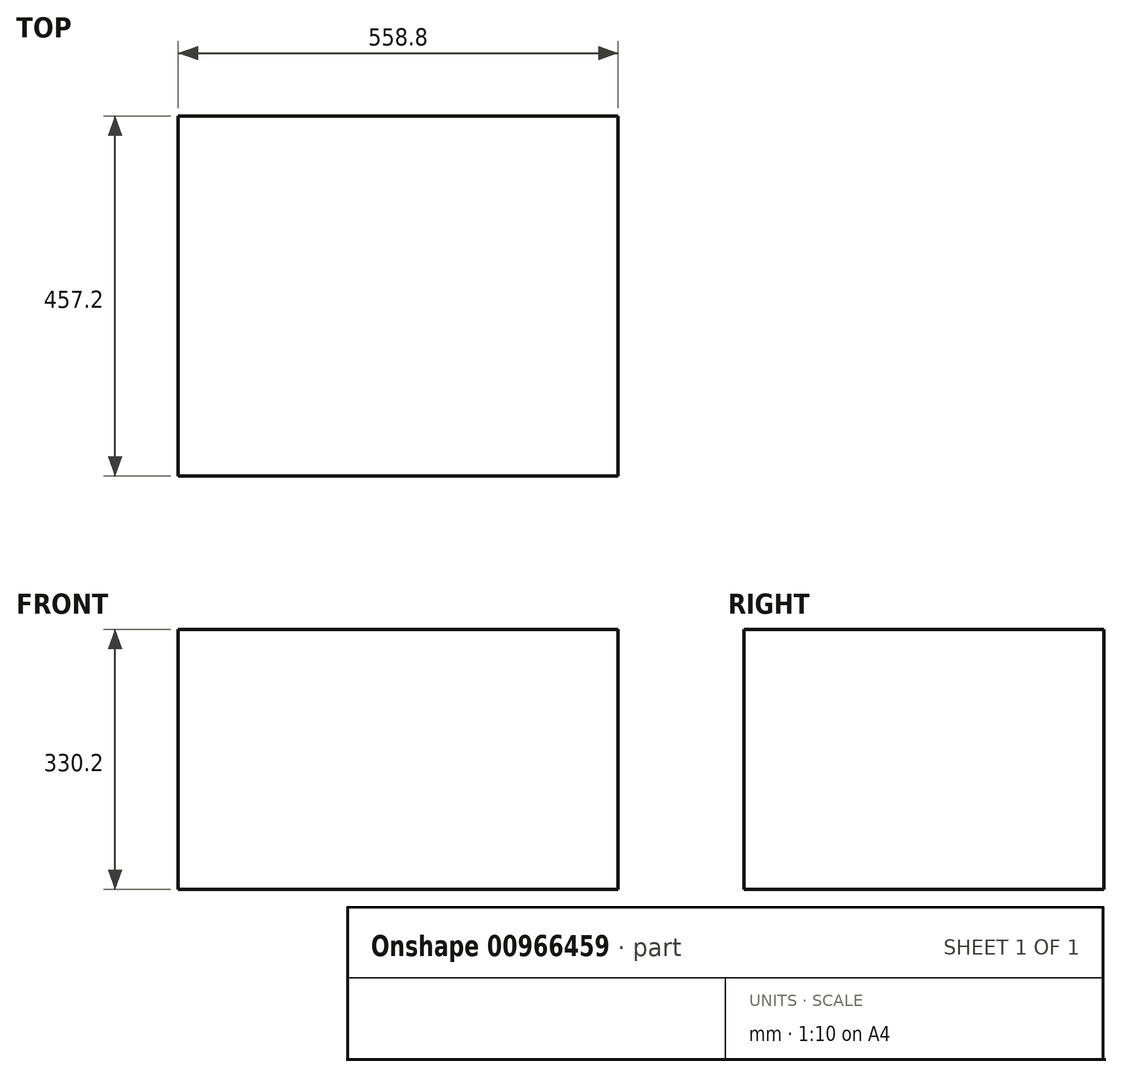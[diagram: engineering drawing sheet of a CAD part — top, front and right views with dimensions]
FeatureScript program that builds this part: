
annotation { "Feature Type Name" : "Feature", "Feature Type Description" : "" }
export const myFeature = defineFeature(function(context is Context, id is Id, definition is map)
    precondition{}
    {
        {
            var Q0;
            Q0=qCreatedBy(makeId("Top.planeOp"),FACE);
            var sketch = newSketch(context, id + "F0", { "sketchPlane" : qUnion([Q0])});
            skLineSegment(sketch, "E0.bottom", {"start": v(279.4, -228.6) * mm, "end": v(-279.4, -228.6) * mm});
            skLineSegment(sketch, "E0.top", {"start": v(279.4, 228.6) * mm, "end": v(-279.4, 228.6) * mm});
            skLineSegment(sketch, "E0.left", {"start": v(279.4, -228.6) * mm, "end": v(279.4, 228.6) * mm});
            skLineSegment(sketch, "E0.right", {"start": v(-279.4, -228.6) * mm, "end": v(-279.4, 228.6) * mm});
            skPoint(sketch, "E0.middle", {"position": v(0, 0) * mm});
            skSolve(sketch);
        }
        {
            var Q0;
            Q0 = qSketchRegion(id + "F0", true);
            extrude(context, id + "F1", {"entities" : qUnion([Q0]), "depth" : 330.2 * mm, "offsetDistance" : 25.4 * mm});
        }
    });
